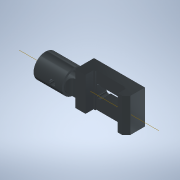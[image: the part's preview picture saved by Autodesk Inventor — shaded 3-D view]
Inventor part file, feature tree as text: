
AUTODESK INVENTOR PART (.ipt)
format: ipt  version: 2022.2 (Build 262287000, 287)  size: 245,248 bytes
history: native  units: mm (DEFAULTED — no unit token found)
features: other x14, sketch x7, extrude x4, hole x1
bodies: Solide1 (feature_tree)
feature tree (26):
  other  "Origine"
  other  "Plan de construction1"
  extrude  "Extrusion1"  Depth=60.0mm TaperAngle=0.0deg
  extrude  "Extrusion2"  Depth=60.0mm TaperAngle=0.0deg
  other  "Plan de construction2"
  sketch  "Esquisse3"
  other  "Révolution1"
  other  "Révolution2"
  extrude  "Extrusion3"  TaperAngle=90.0deg  [1 undecoded]
  other  "Axe de construction1"
  other  "Plan de construction3"
  extrude  "Extrusion4"  TaperAngle=90.0deg  [1 undecoded]
  hole  "Perçage1"  [1 undecoded]
  sketch  "Esquisse8"
  other  "Plan YZ"
  other  "Plan XZ"
  other  "Plan XY"
  other  "Axe X"
  other  "Axe Y"
  other  "Axe Z"
  other  "Point de centre"
  sketch  "Esquisse1"
  sketch  "Esquisse2"
  sketch  "Esquisse5"
  sketch  "Esquisse6"
  sketch  "Esquisse7"
note: 3 required parameter values undecoded (feature->parameter linkage not recoverable at this tier; creation-order binding heuristic only, values carry confidence <= 0.55)
